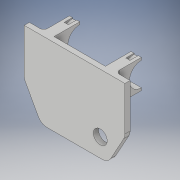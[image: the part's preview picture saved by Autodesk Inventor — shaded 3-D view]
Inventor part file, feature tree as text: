
AUTODESK INVENTOR PART (.ipt)
format: ipt  version: 2019.3 (Build 233278000, 278)  size: 201,728 bytes
history: native  units: mm
features: sketch x6, extrude x3, fillet x2, thicken_offset x2, plane x1, other x1, revolve x1, mirror x1, hole x1, projected_geometry x1
ambient origin geometry x8: Origin, YZ Plane, XZ Plane, XY Plane, X Axis, Y Axis, Z Axis, Center Point
bodies: Solid1 (feature_tree)
feature tree (19):
  extrude  "Extrusion1"  Depth=98.0mm
  extrude  "Extrusion2"  Depth=75.0mm
  extrude  "Extrusion3"  Depth=50.0mm
  plane  "Work Plane1"
  sketch  "Sketch4"  dims[d8=10.0mm d9=28.0mm d10=25.0mm d11=0.0mm d12=22.225mm]
  sketch  "Sketch5"  dims[d13=40.0mm d14=0.0mm d17=4.0mm]
  other  "Work Axis1"
  revolve  "Revolution1"  [1 undecoded]
  mirror  "Mirror1"
  fillet  "Fillet1"  Radius=25.0mm
  fillet  "Fillet2"  Radius=22.225mm
  thicken_offset  "Thicken1"
  thicken_offset  "Thicken2"
  hole  "Hole1"  [1 undecoded]
  sketch  "Sketch1"  dims[d0=98.0mm d1=65.0mm]
  sketch  "Sketch2"  dims[d2=75.0mm d4=45.0mm]
  sketch  "Sketch3"  dims[d5=5.0mm d6=0.0mm d7=50.0mm]
  sketch  "Sketch6"  dims[d18=3.0mm d19=90.0deg d20=9.5mm d21=3.75mm d22=0.5mm d23=0.5mm d24=0.5mm d25=0.5mm d26=18.0mm d27=24.0mm d28=16.0mm d29=16.0mm d30=13.5mm d31=6.0mm d32=4.0mm d33=2.0mm d34=90.0deg d35=8.0mm d36=20.594885mm]
  projected_geometry  "Projected Loop1"
note: 2 required parameter values undecoded (feature->parameter linkage not recoverable at this tier; creation-order binding heuristic only, values carry confidence <= 0.55)